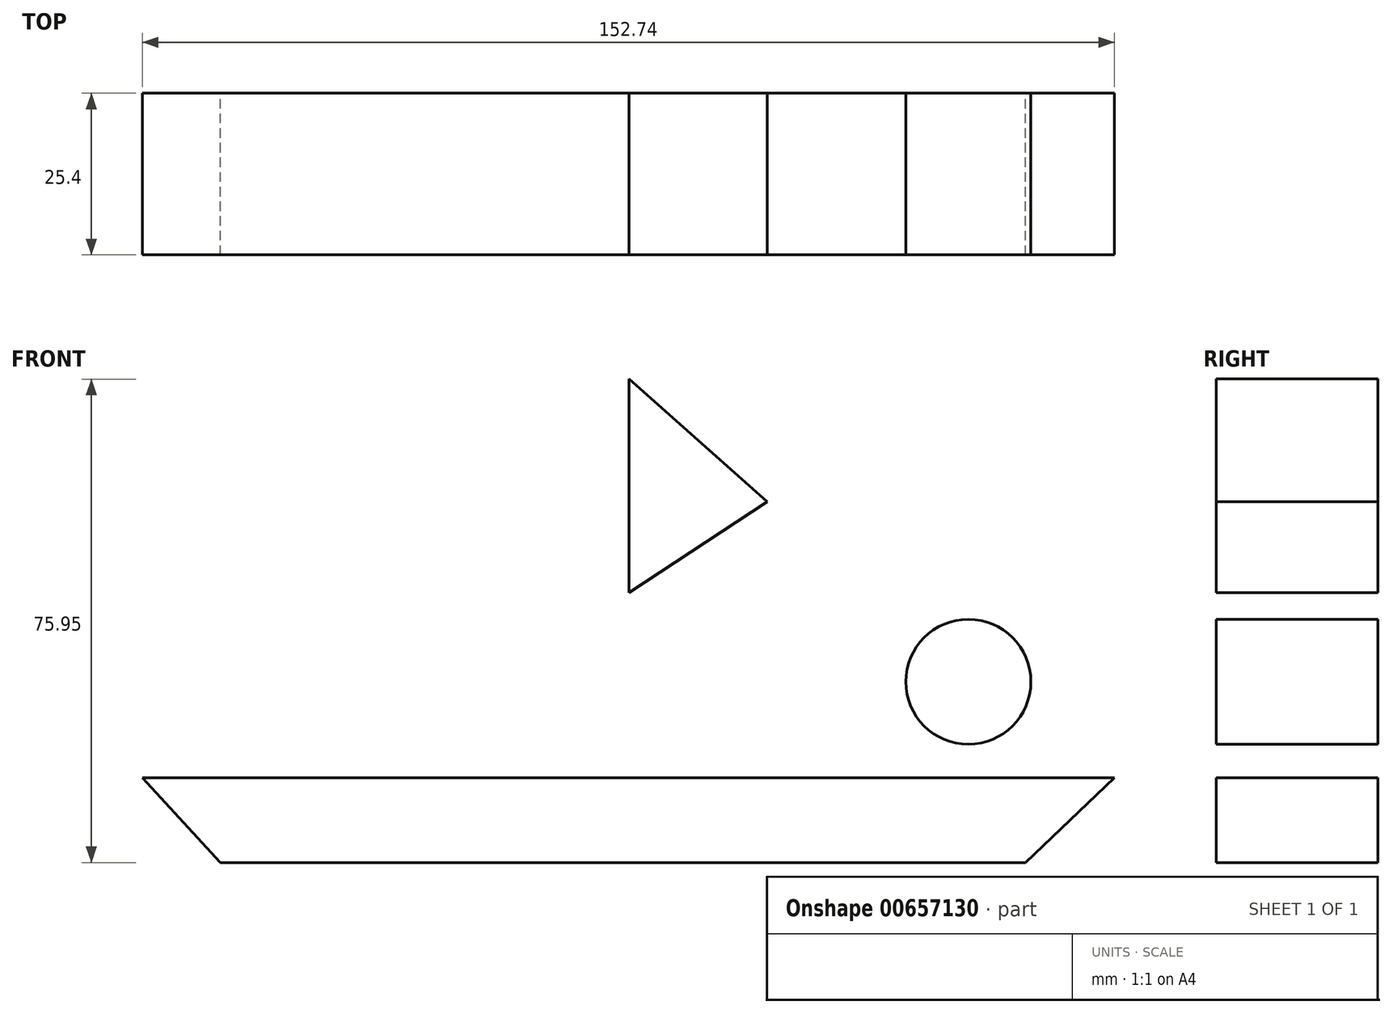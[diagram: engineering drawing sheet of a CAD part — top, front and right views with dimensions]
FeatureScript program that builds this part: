
annotation { "Feature Type Name" : "Feature", "Feature Type Description" : "" }
export const myFeature = defineFeature(function(context is Context, id is Id, definition is map)
    precondition{}
    {
        {
            var Q0;
            Q0=qCreatedBy(makeId("Front.planeOp"),FACE);
            var sketch = newSketch(context, id + "F0", { "sketchPlane" : qUnion([Q0])});
            skLineSegment(sketch, "E0", {"start": v(0, 0) * mm, "end": v(-64.2, 0) * mm});
            skLineSegment(sketch, "E1", {"start": v(-64.2, 0) * mm, "end": v(-76.51, 13.29) * mm});
            skLineSegment(sketch, "E2", {"start": v(-76.51, 13.29) * mm, "end": v(76.23, 13.29) * mm});
            skLineSegment(sketch, "E3", {"start": v(76.23, 13.29) * mm, "end": v(62.25, 0) * mm});
            skLineSegment(sketch, "E4", {"start": v(62.25, 0) * mm, "end": v(0, 0) * mm});
            skLineSegment(sketch, "E5", {"start": v(0, 13.29) * mm, "end": v(0, 75.95) * mm});
            skLineSegment(sketch, "E6", {"start": v(0, 75.95) * mm, "end": v(21.68, 56.65) * mm});
            skLineSegment(sketch, "E7", {"start": v(21.68, 56.65) * mm, "end": v(0, 42.38) * mm});
            skLineSegment(sketch, "E8", {"start": v(0, 42.38) * mm, "end": v(0, 13.29) * mm});
            skLineSegment(sketch, "E9", {"start": v(53.3, 13.29) * mm, "end": v(53.3, 28.4) * mm});
            skLineSegment(sketch, "E10", {"start": v(53.3, 28.4) * mm, "end": v(53.3, 13.29) * mm});
            skCircle(sketch, "E11", {"center": v(53.3, 28.4) * mm, "radius": 9.82 * mm});
            skSolve(sketch);
        }
        {
            var Q0;
            Q0 = qSketchRegion(id + "F0", true);
            extrude(context, id + "F1", {"entities" : qUnion([Q0]), "depth" : 25.4 * mm, "offsetDistance" : 25.4 * mm});
        }
    });
